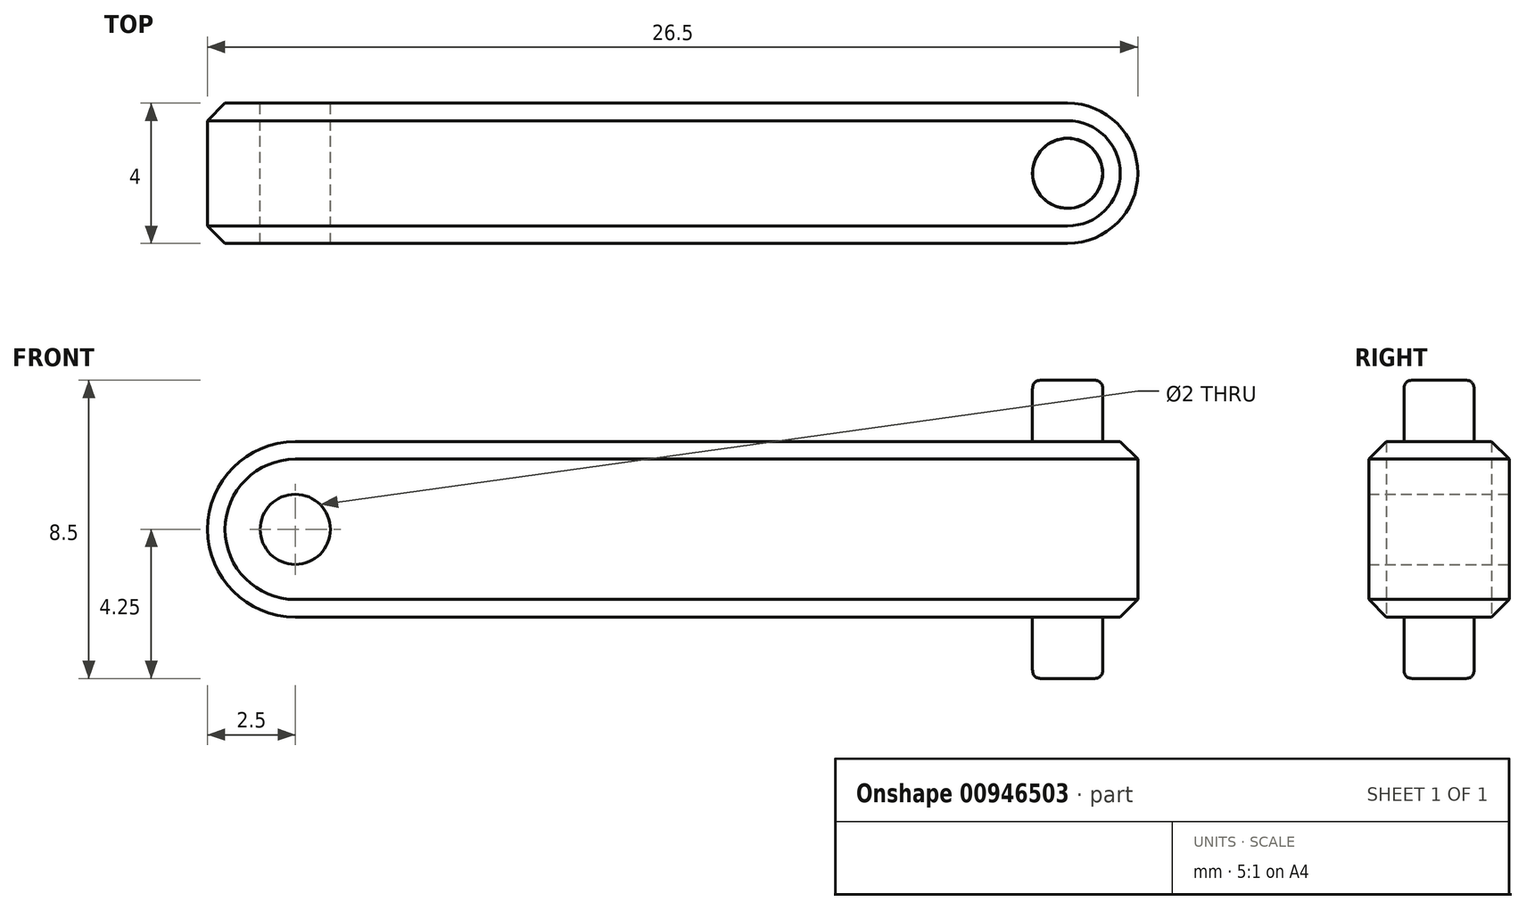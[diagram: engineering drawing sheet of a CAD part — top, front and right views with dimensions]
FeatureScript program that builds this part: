
annotation { "Feature Type Name" : "Feature", "Feature Type Description" : "" }
export const myFeature = defineFeature(function(context is Context, id is Id, definition is map)
    precondition{}
    {
        {
            var Q0;
            Q0=qCreatedBy(makeId("Front.planeOp"),FACE);
            var sketch = newSketch(context, id + "F0", { "sketchPlane" : qUnion([Q0])});
            skLineSegment(sketch, "E0", {"start": v(0, 0) * mm, "end": v(-22, 0) * mm});
            skCircle(sketch, "E1", {"center": v(-22, 0) * mm, "radius": 1 * mm});
            skCircle(sketch, "E2", {"center": v(-22, 0) * mm, "radius": 2.5 * mm});
            skLineSegment(sketch, "E3", {"start": v(-22, 2.5) * mm, "end": v(0, 2.5) * mm});
            skLineSegment(sketch, "E4", {"start": v(0, 2.5) * mm, "end": v(0, -2.5) * mm});
            skLineSegment(sketch, "E5", {"start": v(0, -2.5) * mm, "end": v(-22, -2.5) * mm});
            skSolve(sketch);
        }
        {
            var Q0;
            Q0=qCreatedBy(makeId("Top.planeOp"),FACE);
            var sketch = newSketch(context, id + "F1", { "sketchPlane" : qUnion([Q0])});
            skCircle(sketch, "E6", {"center": v(0, 0) * mm, "radius": 1 * mm});
            skCircle(sketch, "E7", {"center": v(0, 0) * mm, "radius": 2 * mm});
            skSolve(sketch);
        }
        {
            var Q0;
            Q0 = qSketchRegion(id + "F0", true);
            extrude(context, id + "F2", {"entities" : qUnion([Q0]), "depth" : 2 * mm, "offsetDistance" : 25 * mm, "hasSecondDirection" : true, "secondDirectionOppositeDirection" : true, "secondDirectionDepth" : 2 * mm});
        }
        {
            var Q0;
            Q0=makeQuery(id+"F1.imprint","IMPRINT",FACE,{"disambiguationData":[TD([[makeQuery(id+"F1.imprint","IMPRINT",EDGE,{"derivedFrom":sQuery(id+"F1.wireOp",EDGE,"E6")}),1.0]])]});
            var Q1;
            Q1=sQuery(id+"F1.wireOp",EDGE,"E7");
            var Q2;
            Q2=sQuery(id+"F1.wireOp",EDGE,"E6");
            extrude(context, id + "F3", {"entities" : qUnion([Q0]), "operationType" : NewBodyOperationType.ADD, "surfaceEntities" : qUnion([Q1, Q2]), "oppositeDirection" : true, "depth" : 4.25 * mm, "offsetDistance" : 25 * mm, "hasSecondDirection" : true, "secondDirectionOppositeDirection" : false, "secondDirectionDepth" : 4.25 * mm});
        }
        {
            var Q0;
            Q0 = qSketchRegion(id + "F1", true);
            extrude(context, id + "F4", {"entities" : qUnion([Q0]), "operationType" : NewBodyOperationType.ADD, "depth" : 2.5 * mm, "offsetDistance" : 25 * mm, "hasSecondDirection" : true, "secondDirectionOppositeDirection" : true, "secondDirectionDepth" : 2.5 * mm});
        }
        {
            var Q0;
            Q0=makeQuery(id+"F2.opExtrude","CAP_EDGE",EDGE,{"disambiguationData":[OSD([sQuery(id+"F0.wireOp",EDGE,"E3")])],"isStart":false});
            chamfer(context, id + "F5", {"entities" : qUnion([Q0]), "width" : 0.5 * mm, "tangentPropagation" : true});
        }
        {
            var Q0;
            Q0=makeQuery(id+"F3.opExtrude","CAP_EDGE",EDGE,{"disambiguationData":[OSD([sQuery(id+"F1.wireOp",EDGE,"E6")])],"isStart":true});
            var Q1;
            Q1=makeQuery(id+"F3.opExtrude","CAP_EDGE",EDGE,{"disambiguationData":[OSD([sQuery(id+"F1.wireOp",EDGE,"E6")])],"isStart":false});
            fillet(context, id + "F6", {"entities" : qUnion([Q0, Q1]), "tangentPropagation" : true, "crossSection" : FilletCrossSection.CURVATURE, "radius" : 0.25 * mm, "magnitude" : 0.5, "defaultsChanged" : false, "vertexSettings" : []});
        }
    });
